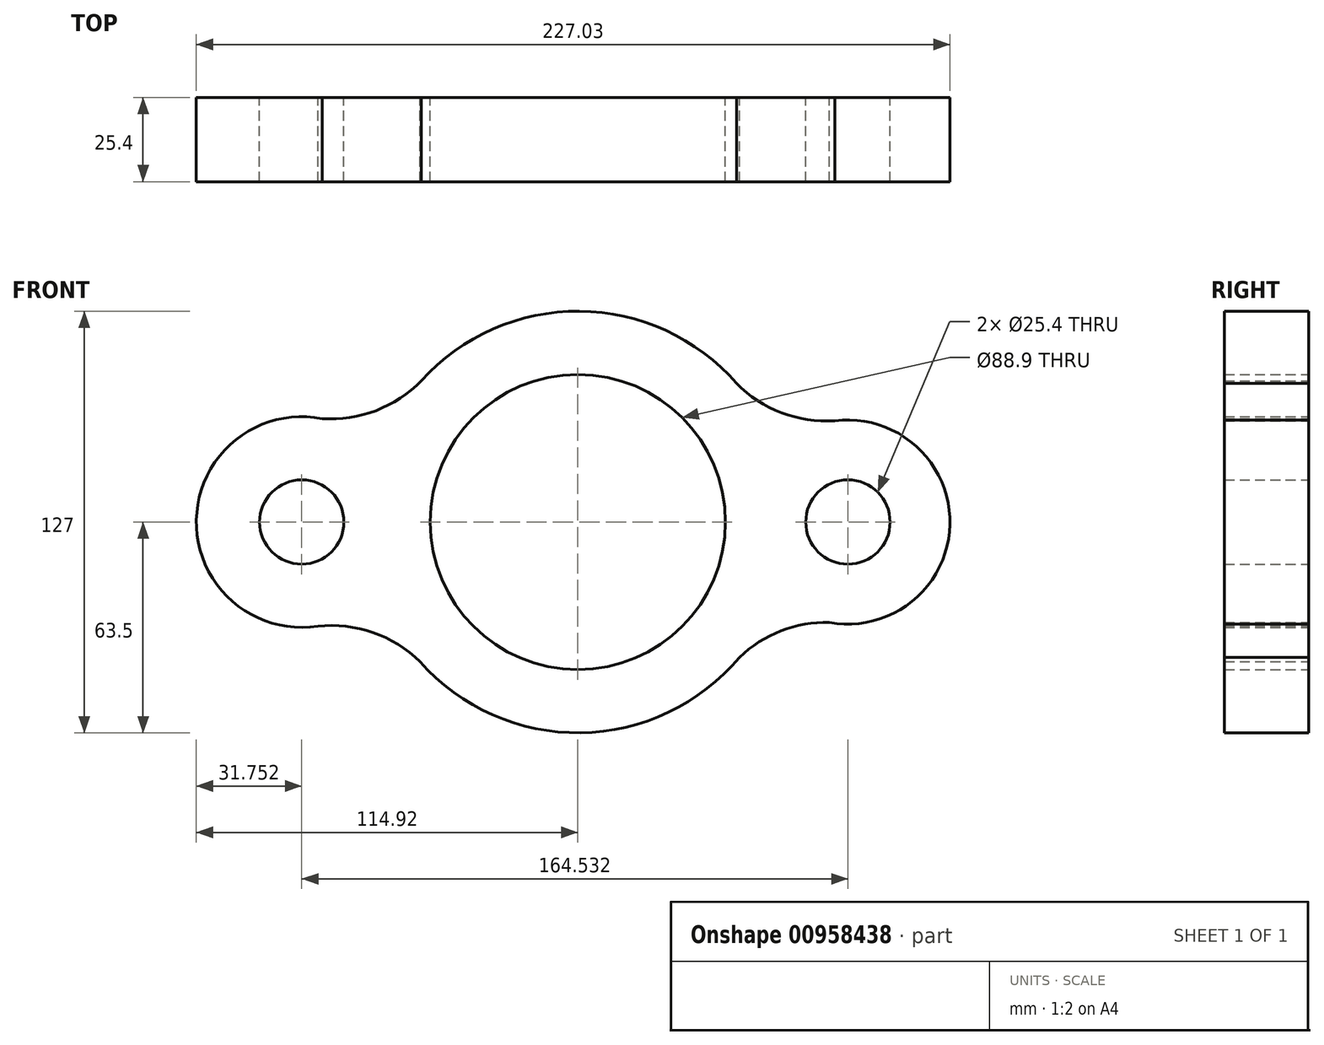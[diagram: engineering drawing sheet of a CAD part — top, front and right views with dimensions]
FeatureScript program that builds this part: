
annotation { "Feature Type Name" : "Feature", "Feature Type Description" : "" }
export const myFeature = defineFeature(function(context is Context, id is Id, definition is map)
    precondition{}
    {
        {
            var Q0;
            Q0=qCreatedBy(makeId("Front.planeOp"),FACE);
            var sketch = newSketch(context, id + "F0", { "sketchPlane" : qUnion([Q0])});
            skCircle(sketch, "E0", {"center": v(0, 0) * mm, "radius": 44.45 * mm});
            skArc(sketch, "E1", {"start": v(-47.56, -42.07) * mm, "mid": v(0.88, -63.5) * mm, "end": v(48.72, -40.73) * mm});
            skArc(sketch, "E2", {"start": v(-77.02, 31.15) * mm, "mid": v(-114.91, 0.66) * mm, "end": v(-78.32, -31.38) * mm});
            skPoint(sketch, "E2.first.point", {"position": v(-113.85, 8.18) * mm});
            skPoint(sketch, "E2.second.point", {"position": v(-110.05, -16.9) * mm});
            skPoint(sketch, "E2.third.point", {"position": v(-90.86, -30.8) * mm});
            skArc(sketch, "E3", {"start": v(75.82, -30.24) * mm, "mid": v(112.1, -0.8) * mm, "end": v(77.4, 30.49) * mm});
            skCircle(sketch, "E4", {"center": v(-83.17, 0) * mm, "radius": 12.7 * mm});
            skCircle(sketch, "E5", {"center": v(81.36, 0) * mm, "radius": 12.7 * mm});
            skArc(sketch, "E6", {"start": v(-81.35, 31.7) * mm, "mid": v(-62.03, 33.13) * mm, "end": v(-45.9, 43.88) * mm});
            skArc(sketch, "E7", {"start": v(-47.56, -42.07) * mm, "mid": v(-62.5, -33.02) * mm, "end": v(-79.91, -31.58) * mm});
            skArc(sketch, "E8", {"start": v(45.93, 43.85) * mm, "mid": v(61.11, 33.02) * mm, "end": v(79.61, 30.7) * mm});
            skArc(sketch, "E9.trimOffspring", {"start": v(47.8, 41.8) * mm, "mid": v(0.52, 63.5) * mm, "end": v(-47.1, 42.58) * mm});
            skArc(sketch, "E10", {"start": v(75.82, -30.24) * mm, "mid": v(61.23, -32.8) * mm, "end": v(48.72, -40.73) * mm});
            skSolve(sketch);
        }
        {
            var Q0;
            Q0 = qSketchRegion(id + "F0", true);
            extrude(context, id + "F1", {"entities" : qUnion([Q0]), "depth" : 25.4 * mm, "offsetDistance" : 25.4 * mm});
        }
    });
